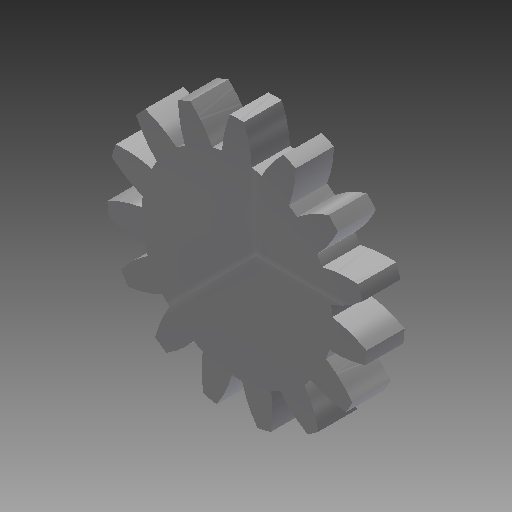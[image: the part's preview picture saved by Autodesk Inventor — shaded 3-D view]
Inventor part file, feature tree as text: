
AUTODESK INVENTOR PART (.ipt)
format: ipt  version: 2017 (Build 210142000, 142)  size: 197,120 bytes
history: native  units: mm (DEFAULTED — no unit token found)
features: plane x3, other x3, sketch x2, extrude x1
ambient origin geometry x8: Origin, YZ Plane, XZ Plane, XY Plane, X Axis, Y Axis, Z Axis, Center Point
bodies: Solid1 (feature_tree)
feature tree (9):
  extrude  "Extrusion1"  Depth=6.35mm TaperAngle=0.0deg
  plane  "Work Plane1"
  plane  "Work Plane2"
  plane  "Work Plane3"
  other  "Spur Gear"
  sketch  "Sketch1"  dims[d0=43.18mm d1=6.35mm d2=0.0mm]
  sketch  "Sketch2"  dims[d3=38.1mm d4=76.2mm d5=0.0mm d6=0.0mm d7=2.094395mm d9=0.0mm d14=0.0mm d15=171.45mm d16=0.0mm d17=0.0mm d18=0.0mm d19=171.45mm]
  other  "Srf1"
  other  "Pitch Diameter"
